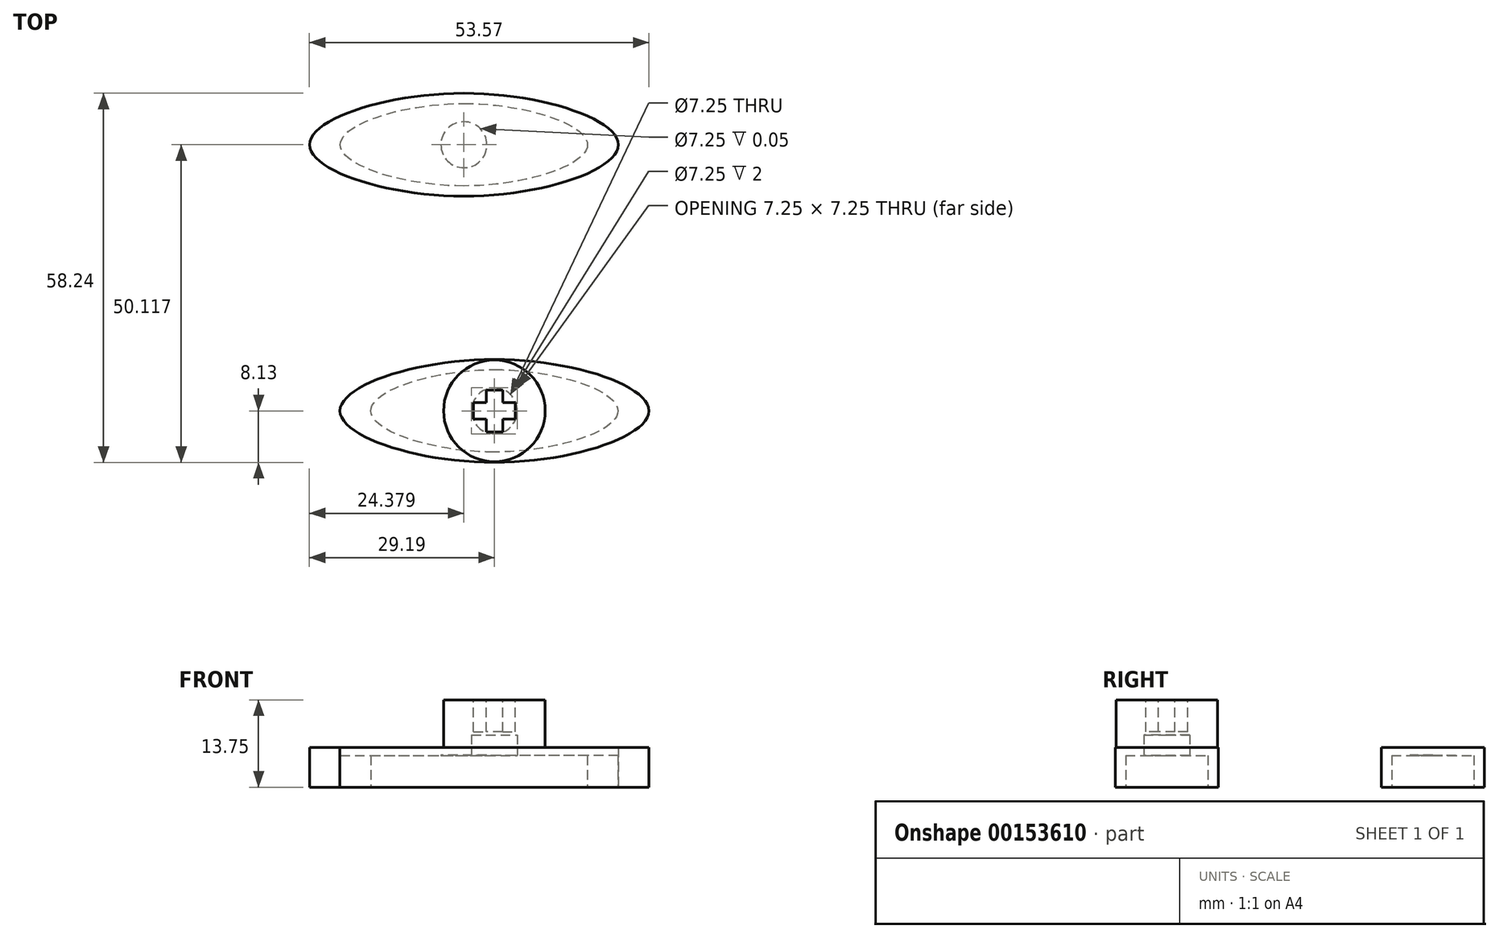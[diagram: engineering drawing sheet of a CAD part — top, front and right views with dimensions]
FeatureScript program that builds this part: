
annotation { "Feature Type Name" : "Feature", "Feature Type Description" : "" }
export const myFeature = defineFeature(function(context is Context, id is Id, definition is map)
    precondition{}
    {
        {
            var Q0;
            Q0=qCreatedBy(makeId("Top.planeOp"),FACE);
            var sketch = newSketch(context, id + "F0", { "sketchPlane" : qUnion([Q0])});
            skLineSegment(sketch, "E0", {"start": v(0, 0) * mm, "end": v(0, 6.5) * mm});
            skLineSegment(sketch, "E1", {"start": v(0, 0) * mm, "end": v(0, -6.5) * mm});
            skLineSegment(sketch, "E2", {"start": v(0, 0) * mm, "end": v(19.5, 0) * mm});
            skLineSegment(sketch, "E3", {"start": v(0, 0) * mm, "end": v(-19.5, 0) * mm});
            skFitSpline(sketch, "E4", {"points": [v(-19.5, 0) * mm, v(0, 6.5) * mm, v(19.5, 0) * mm, v(0, -6.5) * mm, v(-19.5, 0) * mm]});
            skSolve(sketch);
        }
        {
            var Q0;
            {var subQ0=sQuery(id+"F0.wireOp",EDGE,"E0");Q0=makeQuery(id+"F0.imprint","IMPRINT",FACE,{"disambiguationData":[TD([[makeQuery(id+"F0.imprint","IMPRINT",EDGE,{"derivedFrom":subQ0}),1.0]])]});}
            var Q1;
            {var subQ0=sQuery(id+"F0.wireOp",EDGE,"E0");Q1=makeQuery(id+"F0.imprint","IMPRINT",FACE,{"disambiguationData":[TD([[makeQuery(id+"F0.imprint","IMPRINT",EDGE,{"derivedFrom":subQ0}),-1.0]])]});}
            var Q2;
            {var subQ0=sQuery(id+"F0.wireOp",EDGE,"E1");Q2=makeQuery(id+"F0.imprint","IMPRINT",FACE,{"disambiguationData":[TD([[makeQuery(id+"F0.imprint","IMPRINT",EDGE,{"derivedFrom":subQ0}),1.0]])]});}
            var Q3;
            {var subQ0=sQuery(id+"F0.wireOp",EDGE,"E1");Q3=makeQuery(id+"F0.imprint","IMPRINT",FACE,{"disambiguationData":[TD([[makeQuery(id+"F0.imprint","IMPRINT",EDGE,{"derivedFrom":subQ0}),-1.0]])]});}
            extrude(context, id + "F1", {"entities" : qUnion([Q0, Q1, Q2, Q3]), "depth" : 5 * mm});
        }
        {
            var Q0;
            Q0=makeQuery(id+"F1.opExtrude","SWEPT_BODY",BODY,{"disambiguationData":[OSD([sQuery(id+"F0.wireOp",EDGE,"E4")])]});
            var Q1;
            Q1=qCreatedBy(makeId("Origin.pointOp"),VERTEX);
            transform(context, id + "F2", {"entities" : qUnion([Q0]), "transformType" : TransformType.SCALE_UNIFORMLY, "scale" : 1.25, "scalePoint" : qUnion([Q1]), "makeCopy" : true});
        }
        {
            var Q0;
            Q0=makeQuery(id+"F2.opPattern","COPY",FACE,{"derivedFrom":makeQuery(id+"F1.opExtrude","CAP_FACE",FACE,{"disambiguationData":[OSD([sQuery(id+"F0.wireOp",EDGE,"E4")])],"isStart":false}),"instanceName":"1"});
            var sketch = newSketch(context, id + "F3", { "sketchPlane" : qUnion([Q0])});
            skCircle(sketch, "E5", {"center": v(0, 0) * mm, "radius": 8.02 * mm});
            skSolve(sketch);
        }
        {
            var Q0;
            Q0 = qSketchRegion(id + "F3", true);
            var Q1;
            Q1=makeQuery(id+"F3.imprint","IMPRINT",FACE,{"disambiguationData":[TD([[makeQuery(id+"F3.imprint","IMPRINT",EDGE,{"derivedFrom":sQuery(id+"F3.wireOp",EDGE,"E5")}),1.0]])]});
            extrude(context, id + "F4", {"entities" : qUnion([Q0, Q1]), "depth" : 7.5 * mm});
        }
        {
            var Q0;
            Q0=makeQuery(id+"F1.opExtrude","SWEPT_BODY",BODY,{"disambiguationData":[OSD([sQuery(id+"F0.wireOp",EDGE,"E4")])]});
            var Q1;
            Q1=makeQuery(id+"F2.opPattern","COPY",BODY,{"derivedFrom":makeQuery(id+"F1.opExtrude","SWEPT_BODY",BODY,{"disambiguationData":[OSD([sQuery(id+"F0.wireOp",EDGE,"E4")])]}),"instanceName":"1"});
            booleanBodies(context, id + "F5", {"operationType" : BooleanOperationType.SUBTRACTION, "tools" : qUnion([Q0]), "targets" : qUnion([Q1])});
        }
        {
            var Q0;
            Q0=makeQuery(id+"F4.opExtrude","CAP_FACE",FACE,{"disambiguationData":[OSD([sQuery(id+"F3.wireOp",EDGE,"E5")])],"isStart":false});
            var sketch = newSketch(context, id + "F6", { "sketchPlane" : qUnion([Q0])});
            skLineSegment(sketch, "E6.bottom", {"start": v(1.3, 3.3) * mm, "end": v(-1.3, 3.3) * mm});
            skLineSegment(sketch, "E6.top", {"start": v(1.3, -3.3) * mm, "end": v(-1.3, -3.3) * mm});
            skLineSegment(sketch, "E6.left", {"start": v(1.3, 3.3) * mm, "end": v(1.3, -3.3) * mm});
            skLineSegment(sketch, "E6.right", {"start": v(-1.3, 3.3) * mm, "end": v(-1.3, -3.3) * mm});
            skPoint(sketch, "E6.middle", {"position": v(0, 0) * mm});
            skSolve(sketch);
        }
        {
            var Q0;
            Q0=qCreatedBy(makeId("Front.planeOp"),FACE);
            var sketch = newSketch(context, id + "F7", { "sketchPlane" : qUnion([Q0])});
            skLineSegment(sketch, "E7", {"start": v(0, 0) * mm, "end": v(0, 13.86) * mm});
            skSolve(sketch);
        }
        {
            var Q0;
            Q0=makeQuery(id+"F6.imprint","IMPRINT",FACE,{"disambiguationData":[TD([[makeQuery(id+"F6.imprint","IMPRINT",EDGE,{"derivedFrom":sQuery(id+"F6.wireOp",EDGE,"E6.bottom")}),1.0]])]});
            extrude(context, id + "F8", {"entities" : qUnion([Q0]), "oppositeDirection" : true, "depth" : 5 * mm});
        }
        {
            var Q0;
            Q0=makeQuery(id+"F8.opExtrude","SWEPT_BODY",BODY,{"disambiguationData":[OSD([sQuery(id+"F6.wireOp",EDGE,"E6.bottom"),sQuery(id+"F6.wireOp",EDGE,"E6.top"),sQuery(id+"F6.wireOp",EDGE,"E6.left"),sQuery(id+"F6.wireOp",EDGE,"E6.right")])]});
            var Q1;
            Q1=qCreatedBy(makeId("Origin.pointOp"),VERTEX);
            var Q2;
            Q2=sQuery(id+"F7.wireOp",EDGE,"E7");
            transform(context, id + "F9", {"entities" : qUnion([Q0]), "transformType" : TransformType.ROTATION, "transformAxis" : qUnion([Q2]), "angle" : 90 * degree, "makeCopy" : true});
        }
        {
            var Q0;
            Q0=makeQuery(id+"F8.opExtrude","SWEPT_BODY",BODY,{"disambiguationData":[OSD([sQuery(id+"F6.wireOp",EDGE,"E6.bottom"),sQuery(id+"F6.wireOp",EDGE,"E6.top"),sQuery(id+"F6.wireOp",EDGE,"E6.left"),sQuery(id+"F6.wireOp",EDGE,"E6.right")])]});
            var Q1;
            Q1=makeQuery(id+"F9.opPattern","COPY",BODY,{"derivedFrom":makeQuery(id+"F8.opExtrude","SWEPT_BODY",BODY,{"disambiguationData":[OSD([sQuery(id+"F6.wireOp",EDGE,"E6.bottom"),sQuery(id+"F6.wireOp",EDGE,"E6.top"),sQuery(id+"F6.wireOp",EDGE,"E6.left"),sQuery(id+"F6.wireOp",EDGE,"E6.right")])]}),"instanceName":"1"});
            var Q2;
            Q2=makeQuery(id+"F4.opExtrude","SWEPT_BODY",BODY,{"disambiguationData":[OSD([sQuery(id+"F3.wireOp",EDGE,"E5")])]});
            booleanBodies(context, id + "F10", {"operationType" : BooleanOperationType.SUBTRACTION, "tools" : qUnion([Q0, Q1]), "targets" : qUnion([Q2])});
        }
        {
            var Q0;
            Q0=makeQuery(id+"F5.opBoolean","COPY",FACE,{"derivedFrom":makeQuery(id+"F1.opExtrude","CAP_FACE",FACE,{"disambiguationData":[OSD([sQuery(id+"F0.wireOp",EDGE,"E4")])],"isStart":false})});
            var sketch = newSketch(context, id + "F11", { "sketchPlane" : qUnion([Q0])});
            skCircle(sketch, "E8", {"center": v(0, 0) * mm, "radius": 3.62 * mm});
            skSolve(sketch);
        }
        {
            var Q0;
            Q0=qCreatedBy(makeId("Top.planeOp"),FACE);
            var sketch = newSketch(context, id + "F12", { "sketchPlane" : qUnion([Q0])});
            skLineSegment(sketch, "E9", {"start": v(0, 0) * mm, "end": v(-4.81, 41.99) * mm});
            skSolve(sketch);
        }
        {
            var Q0;
            Q0=makeQuery(id+"F11.imprint","IMPRINT",FACE,{"disambiguationData":[TD([[makeQuery(id+"F11.imprint","IMPRINT",EDGE,{"derivedFrom":sQuery(id+"F11.wireOp",EDGE,"E8")}),1.0]])]});
            extrude(context, id + "F13", {"entities" : qUnion([Q0]), "operationType" : NewBodyOperationType.REMOVE, "oppositeDirection" : true, "depth" : 3.25 * mm});
        }
        {
            var Q0;
            Q0=makeQuery(id+"F2.opPattern","COPY",BODY,{"derivedFrom":makeQuery(id+"F1.opExtrude","SWEPT_BODY",BODY,{"disambiguationData":[OSD([sQuery(id+"F0.wireOp",EDGE,"E4")])]}),"instanceName":"1"});
            var Q1;
            Q1=sQuery(id+"F12.wireOp",EDGE,"E9");
            transform(context, id + "F14", {"entities" : qUnion([Q0]), "transformType" : TransformType.TRANSLATION_ENTITY, "oppositeDirectionEntity" : false, "transformLine" : qUnion([Q1]), "makeCopy" : true});
        }
        {
            var Q0;
            Q0=makeQuery(id+"F14.opPattern","COPY",FACE,{"derivedFrom":makeQuery(id+"F2.opPattern","COPY",FACE,{"derivedFrom":makeQuery(id+"F1.opExtrude","CAP_FACE",FACE,{"disambiguationData":[OSD([sQuery(id+"F0.wireOp",EDGE,"E4")])],"isStart":false}),"instanceName":"1"}),"instanceName":"1"});
            var sketch = newSketch(context, id + "F15", { "sketchPlane" : qUnion([Q0])});
            skCircle(sketch, "E10", {"center": v(-4.81, 41.99) * mm, "radius": 4.3 * mm});
            skSolve(sketch);
        }
        {
            var Q0;
            Q0=makeQuery(id+"F15.imprint","IMPRINT",FACE,{"disambiguationData":[TD([[makeQuery(id+"F15.imprint","IMPRINT",EDGE,{"derivedFrom":makeQuery(id+"F14.opPattern","COPY",EDGE,{"derivedFrom":makeQuery(id+"F13.boolean.opBoolean","INTERSECT",EDGE,{"derivedFrom":[makeQuery(id+"F2.opPattern","COPY",FACE,{"derivedFrom":makeQuery(id+"F1.opExtrude","CAP_FACE",FACE,{"disambiguationData":[OSD([sQuery(id+"F0.wireOp",EDGE,"E4")])],"isStart":false}),"instanceName":"1"}),makeQuery(id+"F13.opExtrude","SWEPT_FACE",FACE,{"disambiguationData":[OSD([sQuery(id+"F11.wireOp",EDGE,"E8")])]})]}),"instanceName":"1"})}),1.0]])]});
            extrude(context, id + "F16", {"entities" : qUnion([Q0]), "operationType" : NewBodyOperationType.ADD, "oppositeDirection" : true, "depth" : 1.2 * mm});
        }
    });
